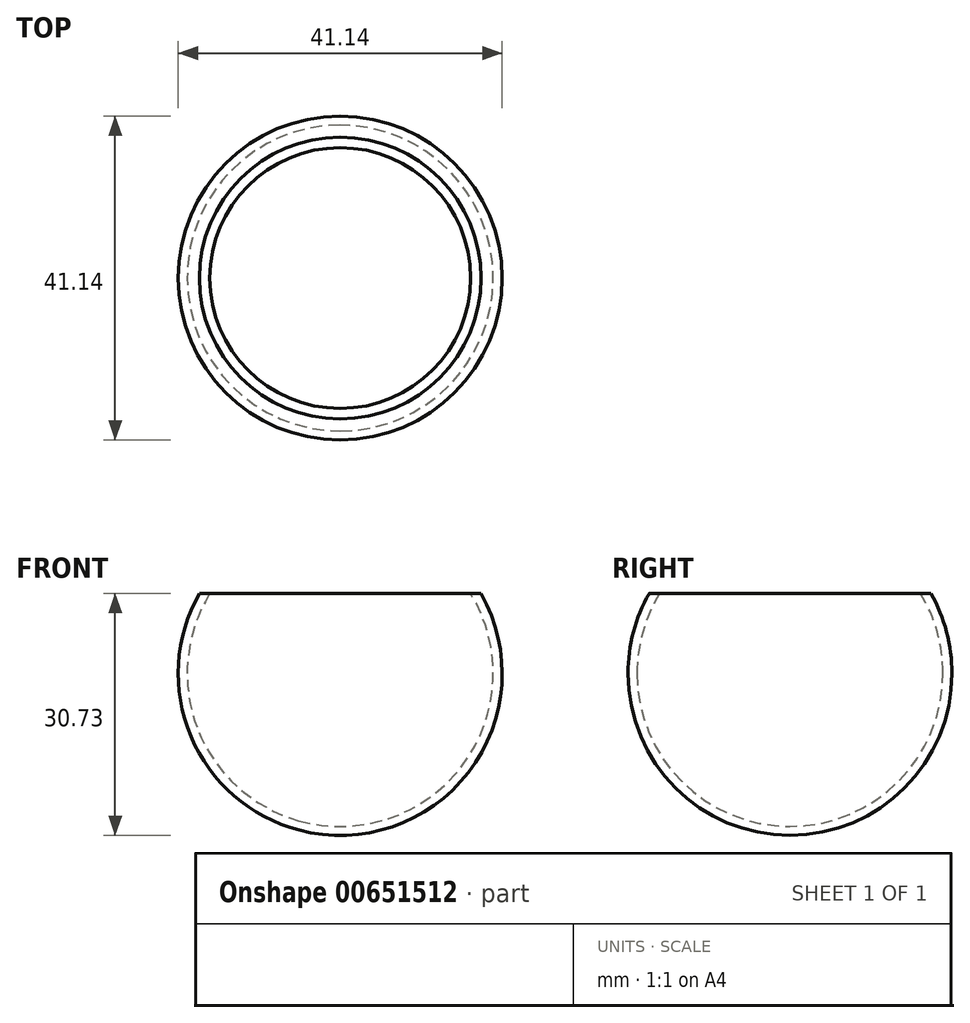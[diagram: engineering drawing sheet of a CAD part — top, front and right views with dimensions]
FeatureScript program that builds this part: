
annotation { "Feature Type Name" : "Feature", "Feature Type Description" : "" }
export const myFeature = defineFeature(function(context is Context, id is Id, definition is map)
    precondition{}
    {
        {
            var Q0;
            Q0=qCreatedBy(makeId("Top.planeOp"),FACE);
            var sketch = newSketch(context, id + "F0", { "sketchPlane" : qUnion([Q0])});
            skCircle(sketch, "E0", {"center": v(0, 0) * mm, "radius": 20.57 * mm});
            skCircle(sketch, "E1", {"center": v(0, 0) * mm, "radius": 19.43 * mm});
            skLineSegment(sketch, "E2", {"start": v(0, 0) * mm, "end": v(0, 20.57) * mm});
            skLineSegment(sketch, "E3", {"start": v(0, 20.57) * mm, "end": v(0, -20.57) * mm});
            skSolve(sketch);
        }
        {
            var Q0;
            {var subQ0=sQuery(id+"F0.wireOp",EDGE,"E3");var subQ1=sQuery(id+"F0.wireOp",EDGE,"E0");var subQ2=makeQuery(id+"F0.imprint","INTERSECT",VERTEX,{"disambiguationData":[OD(0.0)],"derivedFrom":[subQ1,subQ0]});Q0=makeQuery(id+"F0.imprint","IMPRINT",FACE,{"disambiguationData":[TD([[makeQuery(id+"F0.imprint","IMPRINT",EDGE,{"disambiguationData":[TD([[subQ2,1.0]])],"derivedFrom":subQ1}),1.0]])]});}
            var Q1;
            Q1=sQuery(id+"F0.wireOp",EDGE,"E3");
            revolve(context, id + "F1", {"entities" : qUnion([Q0]), "axis" : qUnion([Q1]), "revolveType" : RevolveType.FULL});
        }
        {
            var Q0;
            Q0=qCreatedBy(makeId("Top.planeOp"),FACE);
            cPlane(context, id + "F2", {"entities" : qUnion([Q0]), "cplaneType" : CPlaneType.OFFSET, "offset" : 10.16 * mm, "width" : 152.4 * mm, "height" : 152.4 * mm});
        }
        {
            var Q0;
            Q0=qCreatedBy(id+"F2.planeOp",FACE);
            var sketch = newSketch(context, id + "F3", { "sketchPlane" : qUnion([Q0])});
            skCircle(sketch, "E4", {"center": v(0, 0) * mm, "radius": 20.57 * mm});
            skSolve(sketch);
        }
        {
            var Q0;
            Q0=qSketchRegion(id+"F3",true);
            extrude(context, id + "F4", {"entities" : qUnion([Q0]), "operationType" : NewBodyOperationType.REMOVE, "endBound" : BoundingType.THROUGH_ALL, "depth" : 25.4 * mm});
        }
    });
